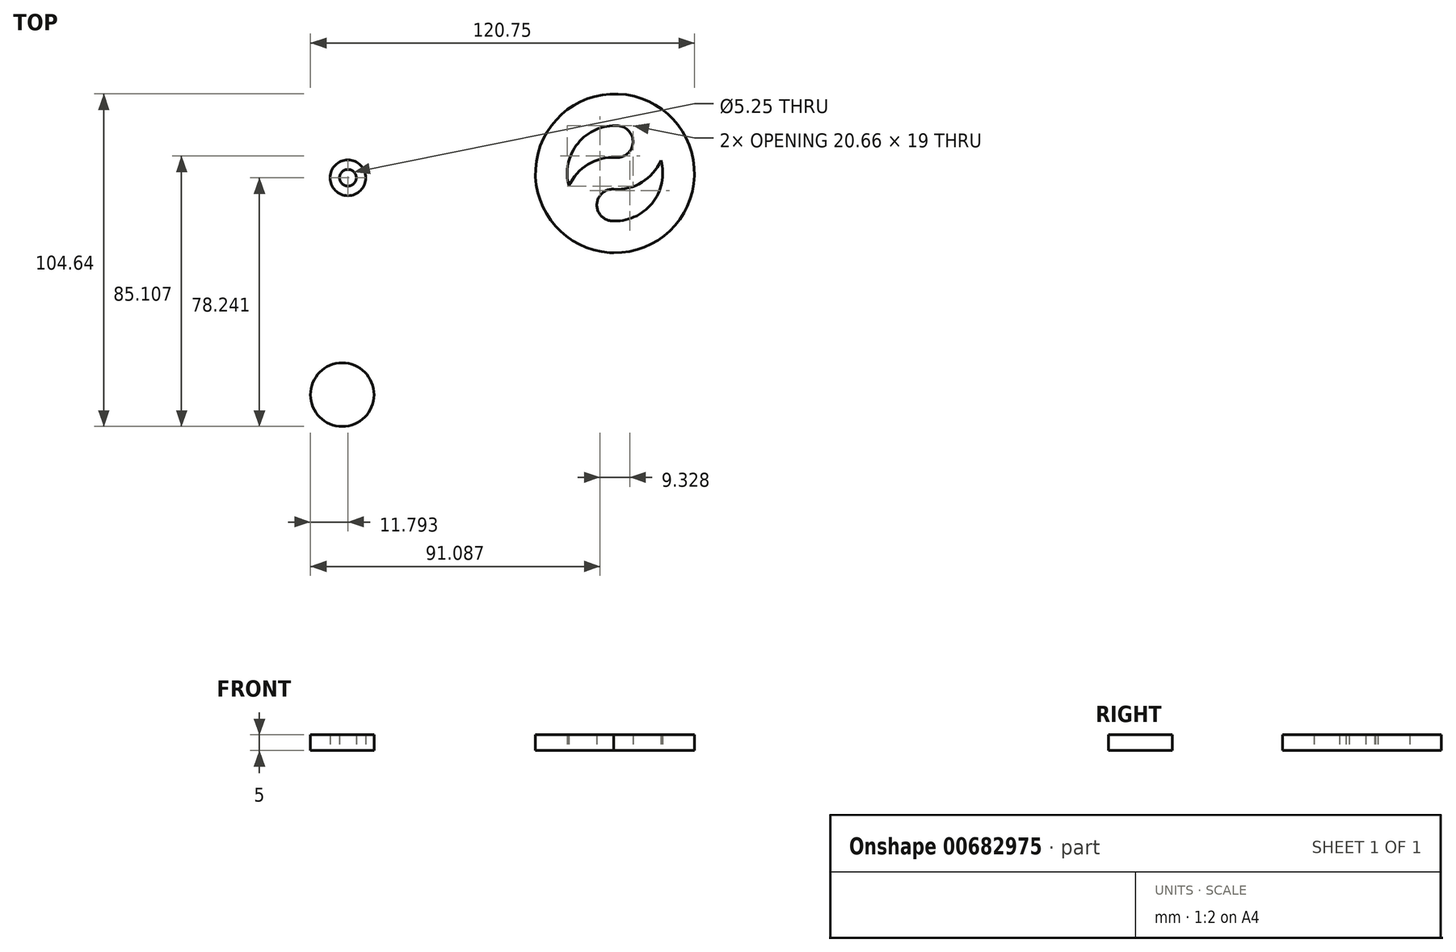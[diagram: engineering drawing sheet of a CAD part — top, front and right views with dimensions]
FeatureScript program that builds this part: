
annotation { "Feature Type Name" : "Feature", "Feature Type Description" : "" }
export const myFeature = defineFeature(function(context is Context, id is Id, definition is map)
    precondition{}
    {
        {
            var Q0;
            Q0=qCreatedBy(makeId("Top.planeOp"),FACE);
            var sketch = newSketch(context, id + "F0", { "sketchPlane" : qUnion([Q0])});
            skArc(sketch, "E0", {"start": v(-1.34, 9.5) * mm, "mid": v(17.8, 20.33) * mm, "end": v(15.43, 42.2) * mm});
            skArc(sketch, "E1", {"start": v(0.01, 29.46) * mm, "mid": v(10.66, 38.76) * mm, "end": v(1.36, 49.42) * mm});
            skArc(sketch, "E2", {"start": v(0.01, 29.46) * mm, "mid": v(-10.64, 20.16) * mm, "end": v(-1.34, 9.5) * mm});
            skPoint(sketch, "E3.trimOffspring.end.orphan", {"position": v(19.46, 44.52) * mm});
            skPoint(sketch, "E4.trimOffspring.end.orphan", {"position": v(10.41, 46.97) * mm});
            skCircle(sketch, "E5.0", {"center": v(0.01, 29.46) * mm, "radius": 25 * mm});
            skArc(sketch, "E6.0", {"start": v(0.35, 34.45) * mm, "mid": v(5.67, 39.1) * mm, "end": v(1.02, 44.43) * mm});
            skArc(sketch, "E7.0", {"start": v(-0.33, 24.47) * mm, "mid": v(-5.65, 19.82) * mm, "end": v(-1, 14.5) * mm});
            skArc(sketch, "E8.0", {"start": v(-1, 14.5) * mm, "mid": v(11.65, 20) * mm, "end": v(14.46, 33.5) * mm});
            skArc(sketch, "E9.0", {"start": v(0.35, 34.45) * mm, "mid": v(-15.66, 19.27) * mm, "end": v(0.77, 4.55) * mm});
            skArc(sketch, "E10.0", {"start": v(-0.33, 24.47) * mm, "mid": v(15.65, 38.43) * mm, "end": v(1.7, 54.4) * mm});
            skArc(sketch, "E11.trimOffspring", {"start": v(1.36, 49.42) * mm, "mid": v(-17.78, 38.59) * mm, "end": v(-15.4, 16.72) * mm});
            skArc(sketch, "E12.trimOffspring", {"start": v(1.02, 44.43) * mm, "mid": v(-11.62, 38.93) * mm, "end": v(-14.44, 25.43) * mm});
            skPoint(sketch, "E13.1.0", {"position": v(-45.88, -14.47) * mm});
            skArc(sketch, "E13.1.1", {"start": v(-21.03, -12.52) * mm, "mid": v(-13.98, -14.61) * mm, "end": v(-12.47, -7.41) * mm});
            skArc(sketch, "E13.1.2", {"start": v(-30, -16.92) * mm, "mid": v(-36.7, -14.64) * mm, "end": v(-38.99, -21.33) * mm});
            skCircle(sketch, "E13.1.3", {"center": v(-25.52, -14.72) * mm, "radius": 25 * mm});
            skArc(sketch, "E13.1.4", {"start": v(-25.52, -14.72) * mm, "mid": v(-11.42, -18.9) * mm, "end": v(-8.4, -4.51) * mm});
            skArc(sketch, "E13.1.5", {"start": v(-25.52, -14.72) * mm, "mid": v(-38.9, -10.15) * mm, "end": v(-43.48, -23.53) * mm});
            skArc(sketch, "E13.1.6", {"start": v(-43.48, -23.53) * mm, "mid": v(-24.53, -34.7) * mm, "end": v(-6.78, -21.7) * mm});
            skArc(sketch, "E13.1.7", {"start": v(-30, -16.92) * mm, "mid": v(-8.86, -23.2) * mm, "end": v(-4.33, -1.6) * mm});
            skArc(sketch, "E13.1.8", {"start": v(-7.56, -5.91) * mm, "mid": v(-26.51, 5.25) * mm, "end": v(-44.26, -7.74) * mm});
            skArc(sketch, "E13.1.9", {"start": v(-21.03, -12.52) * mm, "mid": v(-41.1, -5.66) * mm, "end": v(-47.96, -25.73) * mm});
            skArc(sketch, "E13.1.10", {"start": v(-38.99, -21.33) * mm, "mid": v(-27.9, -29.53) * mm, "end": v(-14.8, -25.22) * mm});
            skArc(sketch, "E13.1.11", {"start": v(-12.05, -8.12) * mm, "mid": v(-23.14, 0.09) * mm, "end": v(-36.24, -4.23) * mm});
            skPoint(sketch, "E13.1.12", {"position": v(-48.29, -5.4) * mm});
            skLineSegment(sketch, "E13.1.13", {"start": v(-8.33, -4.5) * mm, "end": v(-8.4, -4.51) * mm});
            skPoint(sketch, "E13.2.0", {"position": v(35.47, -32.5) * mm});
            skArc(sketch, "E13.2.1", {"start": v(21.36, -11.95) * mm, "mid": v(19.64, -4.8) * mm, "end": v(12.66, -7.1) * mm});
            skArc(sketch, "E13.2.2", {"start": v(29.66, -17.53) * mm, "mid": v(31.02, -24.46) * mm, "end": v(37.96, -23.1) * mm});
            skCircle(sketch, "E13.2.3", {"center": v(25.5, -14.74) * mm, "radius": 25 * mm});
            skArc(sketch, "E13.2.4", {"start": v(25.5, -14.74) * mm, "mid": v(22.78, -0.86) * mm, "end": v(8.9, -3.6) * mm});
            skArc(sketch, "E13.2.5", {"start": v(25.5, -14.74) * mm, "mid": v(28.24, -28.62) * mm, "end": v(42.11, -25.89) * mm});
            skArc(sketch, "E13.2.6", {"start": v(42.11, -25.89) * mm, "mid": v(42.31, -3.9) * mm, "end": v(22.19, 4.98) * mm});
            skArc(sketch, "E13.2.7", {"start": v(29.66, -17.53) * mm, "mid": v(25.57, 3.29) * mm, "end": v(4.75, -0.8) * mm});
            skArc(sketch, "E13.2.8", {"start": v(8.9, -3.6) * mm, "mid": v(8.7, -25.59) * mm, "end": v(28.83, -34.46) * mm});
            skArc(sketch, "E13.2.9", {"start": v(21.36, -11.95) * mm, "mid": v(25.45, -32.77) * mm, "end": v(46.27, -28.67) * mm});
            skArc(sketch, "E13.2.10", {"start": v(37.96, -23.1) * mm, "mid": v(39.53, -9.4) * mm, "end": v(29.24, -0.21) * mm});
            skArc(sketch, "E13.2.11", {"start": v(13.05, -6.38) * mm, "mid": v(11.5, -20.08) * mm, "end": v(21.78, -29.27) * mm});
            skPoint(sketch, "E13.2.12", {"position": v(28.83, -39.12) * mm});
            skPoint(sketch, "E13.center", {"position": v(0, 0) * mm});
            skLineSegment(sketch, "E14.top", {"start": v(0, 75) * mm, "end": v(-60, 75) * mm});
            skLineSegment(sketch, "E14.right", {"start": v(-60, 0) * mm, "end": v(-60, 75) * mm});
            skLineSegment(sketch, "E15.top", {"start": v(0, 75) * mm, "end": v(60, 75) * mm});
            skLineSegment(sketch, "E15.right", {"start": v(60, 0) * mm, "end": v(60, 75) * mm});
            skLineSegment(sketch, "E16.top", {"start": v(0, -75) * mm, "end": v(-60, -75) * mm});
            skLineSegment(sketch, "E16.right", {"start": v(-60, 0) * mm, "end": v(-60, -75) * mm});
            skLineSegment(sketch, "E17.top", {"start": v(0, -75) * mm, "end": v(60, -75) * mm});
            skLineSegment(sketch, "E17.right", {"start": v(60, 0) * mm, "end": v(60, -75) * mm});
            skPoint(sketch, "E18.orphan", {"position": v(60, -0.21) * mm});
            skLineSegment(sketch, "E19.trimOffspring", {"start": v(-0.4, 4.49) * mm, "end": v(-0.4, 4.46) * mm});
            skPoint(sketch, "E20.orphan", {"position": v(-0.19, 14.5) * mm});
            skPoint(sketch, "E21.orphan", {"position": v(8.1, -5.02) * mm});
            skPoint(sketch, "E22.orphan", {"position": v(3.56, -2.95) * mm});
            skCircle(sketch, "E23", {"center": v(-83.95, 28.06) * mm, "radius": 2.62 * mm});
            skCircle(sketch, "E24.0", {"center": v(-83.95, 28.06) * mm, "radius": 5.62 * mm});
            skLineSegment(sketch, "E25", {"start": v(-87.39, 19.79) * mm, "end": v(-80.16, 19.79) * mm});
            skLineSegment(sketch, "E26.0", {"start": v(-87.39, 21.79) * mm, "end": v(-80.16, 21.79) * mm});
            skArc(sketch, "E27", {"start": v(-76.47, 23.29) * mm, "mid": v(-74.8, 20.56) * mm, "end": v(-72.46, 22.73) * mm});
            skArc(sketch, "E28.0", {"start": v(-74.58, 22.62) * mm, "mid": v(-74.53, 22.54) * mm, "end": v(-74.46, 22.6) * mm});
            skCircle(sketch, "E29", {"center": v(-85.74, -40.18) * mm, "radius": 10 * mm});
            skArc(sketch, "E30", {"start": v(-85.74, -40.18) * mm, "mid": v(-80.74, -35.18) * mm, "end": v(-85.74, -30.18) * mm});
            skArc(sketch, "E31", {"start": v(-85.74, -40.18) * mm, "mid": v(-90.74, -45.18) * mm, "end": v(-85.74, -50.18) * mm});
            skArc(sketch, "E32.0", {"start": v(-85.74, -45.18) * mm, "mid": v(-75.74, -35.18) * mm, "end": v(-85.74, -25.18) * mm});
            skArc(sketch, "E33.0", {"start": v(-85.74, -50.18) * mm, "mid": v(-70.74, -35.18) * mm, "end": v(-85.74, -20.18) * mm});
            skArc(sketch, "E34.0", {"start": v(-85.74, -55.18) * mm, "mid": v(-65.74, -35.18) * mm, "end": v(-85.74, -15.18) * mm});
            skLineSegment(sketch, "E35", {"start": v(-60.3, -131.54) * mm, "end": v(59.7, -131.54) * mm});
            skSolve(sketch);
        }
        {
            var Q0;
            Q0=makeQuery(id+"F0.imprint","IMPRINT",FACE,{"disambiguationData":[TD([[makeQuery(id+"F0.imprint","IMPRINT",EDGE,{"derivedFrom":sQuery(id+"F0.wireOp",EDGE,"E23")}),-1.0]])]});
            var Q1;
            {var subQ0=sQuery(id+"F0.wireOp",EDGE,"E30");Q1=makeQuery(id+"F0.imprint","IMPRINT",FACE,{"disambiguationData":[TD([[makeQuery(id+"F0.imprint","IMPRINT",EDGE,{"derivedFrom":subQ0}),-1.0]])]});}
            var Q2;
            {var subQ0=sQuery(id+"F0.wireOp",EDGE,"E30");Q2=makeQuery(id+"F0.imprint","IMPRINT",FACE,{"disambiguationData":[TD([[makeQuery(id+"F0.imprint","IMPRINT",EDGE,{"derivedFrom":subQ0}),1.0]])]});}
            var Q3;
            {var subQ7=sQuery(id+"F0.wireOp",EDGE,"E0");Q3=makeQuery(id+"F0.imprint","IMPRINT",FACE,{"disambiguationData":[TD([[makeQuery(id+"F0.imprint","IMPRINT",EDGE,{"derivedFrom":subQ7}),-1.0]])]});}
            var Q4;
            {var subQ6=sQuery(id+"F0.wireOp",EDGE,"E0");Q4=makeQuery(id+"F0.imprint","IMPRINT",FACE,{"disambiguationData":[TD([[makeQuery(id+"F0.imprint","IMPRINT",EDGE,{"derivedFrom":subQ6}),1.0]])]});}
            extrude(context, id + "F1", {"entities" : qUnion([Q0, Q1, Q2, Q3, Q4]), "depth" : 5 * mm, "offsetDistance" : 25 * mm});
        }
    });
